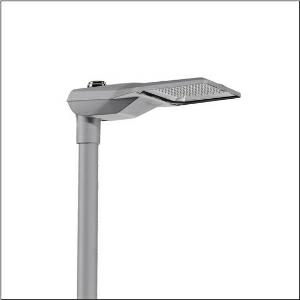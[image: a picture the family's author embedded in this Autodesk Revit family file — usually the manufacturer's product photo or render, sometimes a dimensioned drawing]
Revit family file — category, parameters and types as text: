
# Revit family: streetlight_sl_21_midi___st0_8a_5xe7c47n08lb_a78e
name_source: partatom
category: Lighting Fixtures
units: mm (PartAtom-declared; Revit-internal decimal feet)

## family parameters
Cut with Voids When Loaded = No
Host = Face
Light Source = No
Part Type = Normal
Room Calculation Point = No
Round Connector Dimension = Use Diameter
Shared = No

## types (1)
- --- (1 x LED, 14950 lm, 98.3 W, 4000K)
    Apparent Load = 98 VA
    CIE Flux Codes = 38 75 97 100 100
    Color Rendering = 70
    Color Temperature = 4000K
    Default Elevation = 1800 mm
    Description = Streetlight SL 21 midi, mast luminaire, primary light control with lens, of PMMA, primary optical cover: cover, of toughened safety glass, transparent, light distribution: ST0.8a, light emission: direct distribution, primary light characteristic: asymmetric, installation type: side-entry, LED, 3G 2.5mm², High Power LED, rated luminous flux: 14.950lm, luminous efficacy: 152lm/W, light colour: 740, colour temperature: 4000K, control gear: NEMA (7pin), control: overheat protection, pre-setting: linear dimming characteristic, constant luminous flux control, time-dependent luminous flux control, flexible luminous flux parameterisation, mains connection: 220..240V, AC, 50/60Hz, connection cable pre-assembled, cable length: 10,5m, wiring characteristics: H05VV-F, start of lifetime: 98W, end of service life: 101W, reduction: 45W, luminaire housing, of diecast aluminium (EN AC-44300), powder-coated, Siteco® metallic grey (DB 702S), corrosivity category C5 mid according to DIN EN ISO 12944, multi-level sealing system, sealing non-destructively replaceable, inclination adjustable: 0°, 5°, 10°, 15°, length: 644mm, width: 335mm, height: 110mm, spigot size: 42mm (side-entry), mounting height: 4..8m, protection rating (complete): IP66, insulation class (complete): insulation class I (protective earthing), certification: CE, ENEC, ENEC+, VDE, impact resistance: IK10, permissible operating ambient temperature for outdoor applications: -40..+50°C, standard-compliant lighting for roads and squares, packaging unit: 1 piece

Light Distribution: ST0.8a
    Height = 111 mm
    Lamp = 1 x LED
    Lamp Light Flux = 14950 lm
    Lamp Power = 98.3 W
    Lamp count = 1
    Length = 644 mm
    Luminous efficacy = 152 lm/W
    Manufacturer = Siteco
    ModVariant = No
    Model = 5XE7C47N08LB
    Number of Poles = 1
    OnlyDefault = Yes
    Power Factor = 1
    Product Name = Streetlight SL 21 midi | ST0.8a
    Product group = mast luminaire | pylon top
    ProductGroupID = 6100
    Protection Class = Protection class I
    Protection Degree = IP 66
    RLX_Detail_Level = 1
    RLX_Emergency_Light_Flux = 0 lm
    RLX_Emergency_Type = 0
    RLX_Emergency_Type_DB = No
    RlxData = <blob elided: 26749 chars, md5=7b787067>
    Socket = socket
    Standby Power = 0 W
    System Light Flux = 14950 lm
    System Power = 98 W
    Type Comments = factory setting: luminous flux: 100 % | dim-lin: 254 | 1020 mA
    Type Image = l_1294377.jpg
    URL = http://relux.com
    VarID = @adj_155509
    Voltage = 0 V
    Weight = 0.00 kg
    Width = 336 mm

## geometry (parser evidence)
native form markers: Blend x4, Sweep x9
no freeform markers — native parametric forms only
